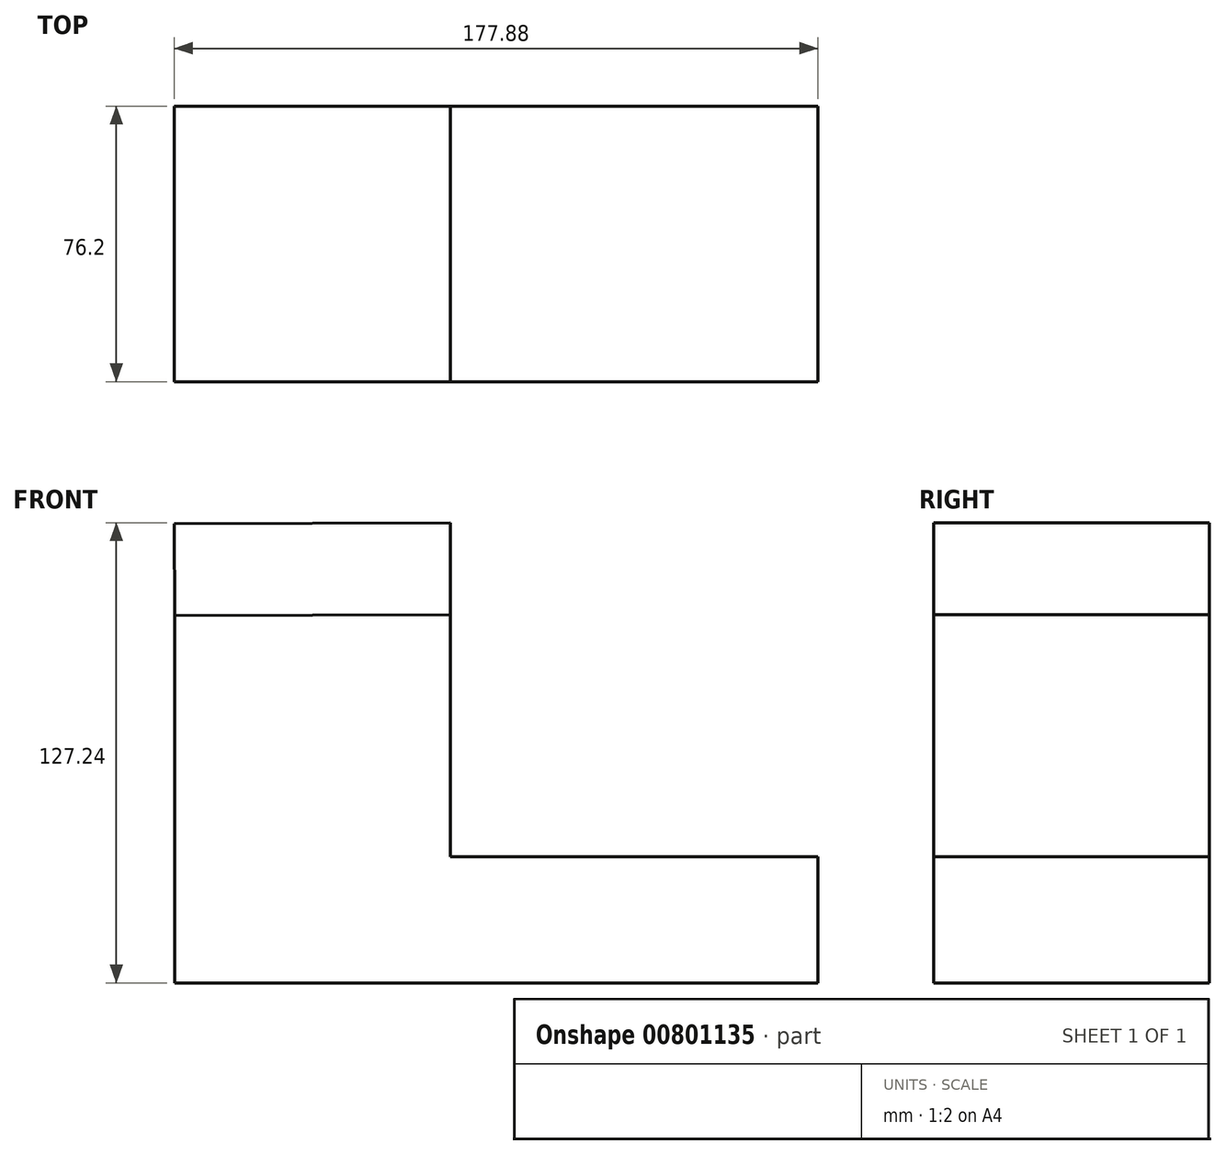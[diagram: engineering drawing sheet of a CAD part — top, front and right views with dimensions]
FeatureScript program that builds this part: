
annotation { "Feature Type Name" : "Feature", "Feature Type Description" : "" }
export const myFeature = defineFeature(function(context is Context, id is Id, definition is map)
    precondition{}
    {
        {
            var Q0;
            Q0=qCreatedBy(makeId("Front.planeOp"),FACE);
            var sketch = newSketch(context, id + "F0", { "sketchPlane" : qUnion([Q0])});
            skLineSegment(sketch, "E0", {"start": v(0, 0) * mm, "end": v(0, 101.6) * mm});
            skLineSegment(sketch, "E1", {"start": v(0, 0) * mm, "end": v(177.8, 0) * mm});
            skLineSegment(sketch, "E2", {"start": v(177.8, 0) * mm, "end": v(177.8, 34.93) * mm});
            skLineSegment(sketch, "E3", {"start": v(177.8, 34.93) * mm, "end": v(76.2, 34.93) * mm});
            skLineSegment(sketch, "E4", {"start": v(76.2, 34.93) * mm, "end": v(76.2, 101.84) * mm});
            skLineSegment(sketch, "E5", {"start": v(0, 101.6) * mm, "end": v(76.2, 101.84) * mm});
            skSolve(sketch);
        }
        {
            var Q0;
            Q0 = qSketchRegion(id + "F0", true);
            extrude(context, id + "F1", {"entities" : qUnion([Q0]), "depth" : 76.2 * mm, "offsetDistance" : 25.4 * mm});
        }
        {
            var Q0;
            Q0=makeQuery(id+"F1.opExtrude","CAP_FACE",FACE,{"disambiguationData":[OSD([sQuery(id+"F0.wireOp",EDGE,"E0"),sQuery(id+"F0.wireOp",EDGE,"E1"),sQuery(id+"F0.wireOp",EDGE,"E2"),sQuery(id+"F0.wireOp",EDGE,"E3"),sQuery(id+"F0.wireOp",EDGE,"E4"),sQuery(id+"F0.wireOp",EDGE,"E5")])],"isStart":false});
            var sketch = newSketch(context, id + "F2", { "sketchPlane" : qUnion([Q0])});
            skLineSegment(sketch, "E6", {"start": v(0, 101.6) * mm, "end": v(-0.08, 127) * mm});
            skLineSegment(sketch, "E7", {"start": v(-0.08, 127) * mm, "end": v(76.2, 127.24) * mm});
            skLineSegment(sketch, "E8", {"start": v(76.2, 127.24) * mm, "end": v(76.2, 101.84) * mm});
            skSolve(sketch);
        }
        {
            var Q0;
            Q0=makeQuery(id+"F2.imprint","IMPRINT",FACE,{"disambiguationData":[TD([[makeQuery(id+"F2.imprint","IMPRINT",EDGE,{"derivedFrom":sQuery(id+"F2.wireOp",EDGE,"E6")}),-1.0]])]});
            extrude(context, id + "F3", {"entities" : qUnion([Q0]), "oppositeDirection" : true, "depth" : 76.2 * mm, "offsetDistance" : 25.4 * mm});
        }
    });
